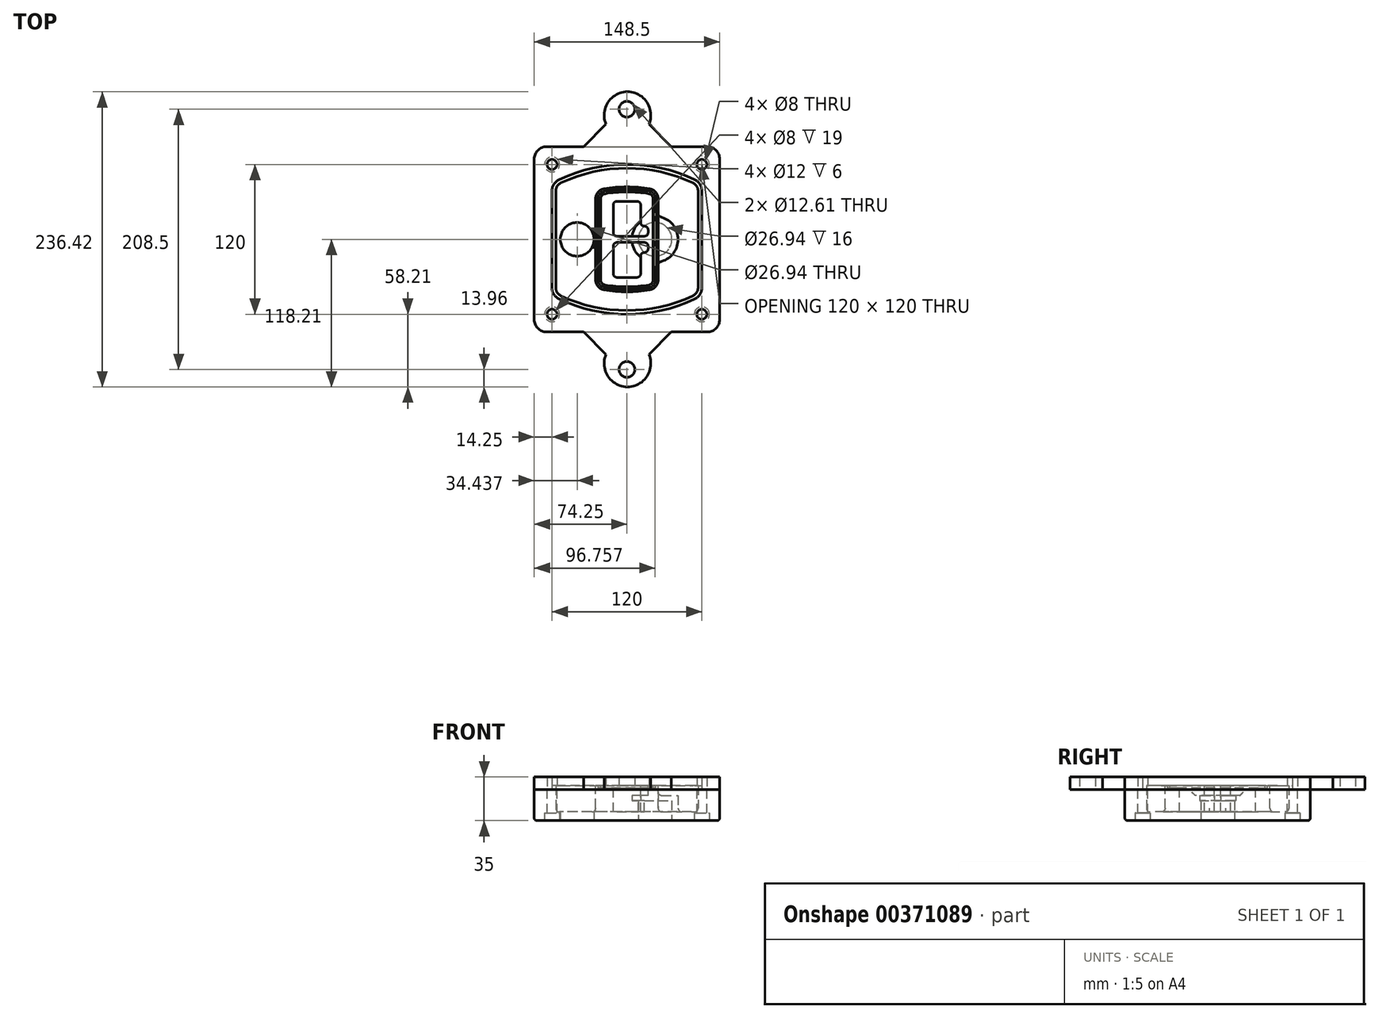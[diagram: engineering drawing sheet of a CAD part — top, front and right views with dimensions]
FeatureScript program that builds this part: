
annotation { "Feature Type Name" : "Feature", "Feature Type Description" : "" }
export const myFeature = defineFeature(function(context is Context, id is Id, definition is map)
    precondition{}
    {
        {
            var Q0;
            Q0=qCreatedBy(makeId("Top.planeOp"),FACE);
            var sketch = newSketch(context, id + "F0", { "sketchPlane" : qUnion([Q0])});
            skPoint(sketch, "E0.rect.middle", {"position": v(0, 0) * mm});
            skLineSegment(sketch, "E1.bottom", {"start": v(-64.25, -74.25) * mm, "end": v(64.25, -74.25) * mm});
            skLineSegment(sketch, "E1.top", {"start": v(-64.25, 74.25) * mm, "end": v(64.25, 74.25) * mm});
            skLineSegment(sketch, "E1.left", {"start": v(-74.25, -64.25) * mm, "end": v(-74.25, 64.25) * mm});
            skLineSegment(sketch, "E1.right", {"start": v(74.25, -64.25) * mm, "end": v(74.25, 64.25) * mm});
            skLineSegment(sketch, "E2", {"start": v(-74.25, 74.25) * mm, "end": v(74.25, -74.25) * mm, "construction": true});
            skLineSegment(sketch, "E3", {"start": v(74.25, 74.25) * mm, "end": v(-74.25, -74.25) * mm, "construction": true});
            skCircle(sketch, "E4", {"center": v(-60, 60) * mm, "radius": 4 * mm});
            skCircle(sketch, "E5", {"center": v(60, 60) * mm, "radius": 4 * mm});
            skCircle(sketch, "E6", {"center": v(60, -60) * mm, "radius": 4 * mm});
            skCircle(sketch, "E7", {"center": v(-60, -60) * mm, "radius": 4 * mm});
            skLineSegment(sketch, "E8", {"start": v(-60, 60) * mm, "end": v(60, 60) * mm, "construction": true});
            skLineSegment(sketch, "E9", {"start": v(60, 60) * mm, "end": v(60, -60) * mm, "construction": true});
            skLineSegment(sketch, "E10", {"start": v(60, -60) * mm, "end": v(-60, -60) * mm, "construction": true});
            skLineSegment(sketch, "E11", {"start": v(-60, -60) * mm, "end": v(-60, 60) * mm, "construction": true});
            skLineSegment(sketch, "E12", {"start": v(-60, 38.83) * mm, "end": v(-60, -38.83) * mm});
            skLineSegment(sketch, "E13", {"start": v(60, 38.83) * mm, "end": v(60, -38.83) * mm});
            skArc(sketch, "E14", {"start": v(54.26, 47.88) * mm, "mid": v(0, 60) * mm, "end": v(-54.26, 47.88) * mm});
            skArc(sketch, "E15", {"start": v(-54.26, -47.88) * mm, "mid": v(0, -60) * mm, "end": v(54.26, -47.88) * mm});
            skLineSegment(sketch, "E16", {"start": v(-60, 0) * mm, "end": v(60, 0) * mm, "construction": true});
            skPoint(sketch, "E17.visualSharp", {"position": v(-60, -45) * mm});
            skArc(sketch, "E17.filletArc", {"start": v(-60, -38.83) * mm, "mid": v(-58.44, -44.2) * mm, "end": v(-54.26, -47.88) * mm});
            skPoint(sketch, "E18.visualSharp", {"position": v(-60, 45) * mm});
            skArc(sketch, "E18.filletArc", {"start": v(-54.26, 47.88) * mm, "mid": v(-58.44, 44.2) * mm, "end": v(-60, 38.83) * mm});
            skPoint(sketch, "E19.visualSharp", {"position": v(60, 45) * mm});
            skArc(sketch, "E19.filletArc", {"start": v(60, 38.83) * mm, "mid": v(58.44, 44.2) * mm, "end": v(54.26, 47.88) * mm});
            skPoint(sketch, "E20.visualSharp", {"position": v(60, -45) * mm});
            skArc(sketch, "E20.filletArc", {"start": v(54.26, -47.88) * mm, "mid": v(58.44, -44.2) * mm, "end": v(60, -38.83) * mm});
            skPoint(sketch, "E21.visualSharp", {"position": v(-74.25, 74.25) * mm});
            skArc(sketch, "E21.filletArc", {"start": v(-64.25, 74.25) * mm, "mid": v(-71.32, 71.32) * mm, "end": v(-74.25, 64.25) * mm});
            skPoint(sketch, "E22.visualSharp", {"position": v(74.25, 74.25) * mm});
            skArc(sketch, "E22.filletArc", {"start": v(74.25, 64.25) * mm, "mid": v(71.32, 71.32) * mm, "end": v(64.25, 74.25) * mm});
            skPoint(sketch, "E23.visualSharp", {"position": v(74.25, -74.25) * mm});
            skArc(sketch, "E23.filletArc", {"start": v(64.25, -74.25) * mm, "mid": v(71.32, -71.32) * mm, "end": v(74.25, -64.25) * mm});
            skPoint(sketch, "E24.visualSharp", {"position": v(-74.25, -74.25) * mm});
            skArc(sketch, "E24.filletArc", {"start": v(-74.25, -64.25) * mm, "mid": v(-71.32, -71.32) * mm, "end": v(-64.25, -74.25) * mm});
            skArc(sketch, "E25.0", {"start": v(57, 38.83) * mm, "mid": v(55.9, 42.58) * mm, "end": v(52.98, 45.17) * mm});
            skLineSegment(sketch, "E25.1", {"start": v(57, 38.83) * mm, "end": v(57, -38.83) * mm});
            skArc(sketch, "E25.2", {"start": v(52.98, -45.17) * mm, "mid": v(55.9, -42.58) * mm, "end": v(57, -38.83) * mm});
            skArc(sketch, "E25.3", {"start": v(-52.98, -45.17) * mm, "mid": v(0, -57) * mm, "end": v(52.98, -45.17) * mm});
            skArc(sketch, "E25.4", {"start": v(-57, -38.83) * mm, "mid": v(-55.9, -42.58) * mm, "end": v(-52.98, -45.17) * mm});
            skArc(sketch, "E25.5", {"start": v(52.98, 45.17) * mm, "mid": v(0, 57) * mm, "end": v(-52.98, 45.17) * mm});
            skLineSegment(sketch, "E25.6", {"start": v(-57, 38.83) * mm, "end": v(-57, -38.83) * mm});
            skArc(sketch, "E25.7", {"start": v(-52.98, 45.17) * mm, "mid": v(-55.9, 42.58) * mm, "end": v(-57, 38.83) * mm});
            skArc(sketch, "E26.0", {"start": v(-55.96, 51.5) * mm, "mid": v(-61.82, 46.33) * mm, "end": v(-64, 38.83) * mm});
            skArc(sketch, "E26.1", {"start": v(55.96, 51.5) * mm, "mid": v(0, 64) * mm, "end": v(-55.96, 51.5) * mm});
            skArc(sketch, "E26.2", {"start": v(64, 38.83) * mm, "mid": v(61.82, 46.33) * mm, "end": v(55.96, 51.5) * mm});
            skLineSegment(sketch, "E26.3", {"start": v(64, 38.83) * mm, "end": v(64, -38.83) * mm});
            skArc(sketch, "E26.4", {"start": v(55.96, -51.5) * mm, "mid": v(61.82, -46.33) * mm, "end": v(64, -38.83) * mm});
            skLineSegment(sketch, "E26.5", {"start": v(-64, 38.83) * mm, "end": v(-64, -38.83) * mm});
            skArc(sketch, "E26.6", {"start": v(-55.96, -51.5) * mm, "mid": v(0, -64) * mm, "end": v(55.96, -51.5) * mm});
            skArc(sketch, "E26.7", {"start": v(-64, -38.83) * mm, "mid": v(-61.82, -46.33) * mm, "end": v(-55.96, -51.5) * mm});
            skSolve(sketch);
        }
        {
            var Q0;
            Q0=makeQuery(id+"F0.imprint","IMPRINT",FACE,{"disambiguationData":[TD([[makeQuery(id+"F0.imprint","IMPRINT",EDGE,{"derivedFrom":sQuery(id+"F0.wireOp",EDGE,"E1.bottom")}),1.0]])]});
            var Q1;
            Q1=makeQuery(id+"F0.imprint","IMPRINT",FACE,{"disambiguationData":[TD([[makeQuery(id+"F0.imprint","IMPRINT",EDGE,{"derivedFrom":sQuery(id+"F0.wireOp",EDGE,"E12")}),1.0]])]});
            var Q2;
            Q2=makeQuery(id+"F0.imprint","IMPRINT",FACE,{"disambiguationData":[TD([[makeQuery(id+"F0.imprint","IMPRINT",EDGE,{"derivedFrom":sQuery(id+"F0.wireOp",EDGE,"E25.0")}),1.0]])]});
            var Q3;
            Q3=makeQuery(id+"F0.imprint","IMPRINT",FACE,{"disambiguationData":[TD([[makeQuery(id+"F0.imprint","IMPRINT",EDGE,{"derivedFrom":sQuery(id+"F0.wireOp",EDGE,"E12")}),-1.0]])]});
            extrude(context, id + "F1", {"entities" : qUnion([Q0, Q1, Q2, Q3]), "oppositeDirection" : true, "depth" : 25 * mm});
        }
        {
            var Q0;
            Q0=makeQuery(id+"F0.imprint","IMPRINT",FACE,{"disambiguationData":[TD([[makeQuery(id+"F0.imprint","IMPRINT",EDGE,{"derivedFrom":sQuery(id+"F0.wireOp",EDGE,"E12")}),1.0]])]});
            extrude(context, id + "F2", {"entities" : qUnion([Q0]), "operationType" : NewBodyOperationType.ADD, "depth" : 3 * mm});
        }
        {
            var Q0;
            Q0=makeQuery(id+"F0.imprint","IMPRINT",FACE,{"disambiguationData":[TD([[makeQuery(id+"F0.imprint","IMPRINT",EDGE,{"derivedFrom":sQuery(id+"F0.wireOp",EDGE,"E25.0")}),1.0]])]});
            extrude(context, id + "F3", {"entities" : qUnion([Q0]), "operationType" : NewBodyOperationType.REMOVE, "oppositeDirection" : true, "depth" : 18 * mm});
        }
        {
            var Q0;
            Q0=makeQuery(id+"F2.opExtrude","CAP_FACE",FACE,{"disambiguationData":[OSD([sQuery(id+"F0.wireOp",EDGE,"E12"),sQuery(id+"F0.wireOp",EDGE,"E13"),sQuery(id+"F0.wireOp",EDGE,"E14"),sQuery(id+"F0.wireOp",EDGE,"E15"),sQuery(id+"F0.wireOp",EDGE,"E17.filletArc"),sQuery(id+"F0.wireOp",EDGE,"E18.filletArc"),sQuery(id+"F0.wireOp",EDGE,"E19.filletArc"),sQuery(id+"F0.wireOp",EDGE,"E20.filletArc"),sQuery(id+"F0.wireOp",EDGE,"E25.0"),sQuery(id+"F0.wireOp",EDGE,"E25.1"),sQuery(id+"F0.wireOp",EDGE,"E25.2"),sQuery(id+"F0.wireOp",EDGE,"E25.3"),sQuery(id+"F0.wireOp",EDGE,"E25.4"),sQuery(id+"F0.wireOp",EDGE,"E25.5"),sQuery(id+"F0.wireOp",EDGE,"E25.6"),sQuery(id+"F0.wireOp",EDGE,"E25.7")])],"isStart":false});
            var sketch = newSketch(context, id + "F4", { "sketchPlane" : qUnion([Q0])});
            skArc(sketch, "E27.0", {"start": v(-18.34, -40.45) * mm, "mid": v(0, -42) * mm, "end": v(18.34, -40.45) * mm});
            skArc(sketch, "E28.0", {"start": v(18.34, 40.45) * mm, "mid": v(0, 42) * mm, "end": v(-18.34, 40.45) * mm});
            skLineSegment(sketch, "E29", {"start": v(-25, 32.57) * mm, "end": v(-25, -32.57) * mm});
            skLineSegment(sketch, "E30", {"start": v(25, 32.57) * mm, "end": v(25, -32.57) * mm});
            skLineSegment(sketch, "E31", {"start": v(-25, 39.1) * mm, "end": v(25, 39.1) * mm, "construction": true});
            skLineSegment(sketch, "E32", {"start": v(-25, -39.1) * mm, "end": v(25, -39.1) * mm, "construction": true});
            skPoint(sketch, "E33.visualSharp", {"position": v(-25, 39.1) * mm});
            skArc(sketch, "E33.filletArc", {"start": v(-18.34, 40.45) * mm, "mid": v(-23.11, 37.73) * mm, "end": v(-25, 32.57) * mm});
            skPoint(sketch, "E34.visualSharp", {"position": v(25, 39.1) * mm});
            skArc(sketch, "E34.filletArc", {"start": v(25, 32.57) * mm, "mid": v(23.11, 37.73) * mm, "end": v(18.34, 40.45) * mm});
            skPoint(sketch, "E35.visualSharp", {"position": v(25, -39.1) * mm});
            skArc(sketch, "E35.filletArc", {"start": v(18.34, -40.45) * mm, "mid": v(23.11, -37.73) * mm, "end": v(25, -32.57) * mm});
            skPoint(sketch, "E36.visualSharp", {"position": v(-25, -39.1) * mm});
            skArc(sketch, "E36.filletArc", {"start": v(-25, -32.57) * mm, "mid": v(-23.11, -37.73) * mm, "end": v(-18.34, -40.45) * mm});
            skArc(sketch, "E37.0", {"start": v(52.98, 45.17) * mm, "mid": v(0, 57) * mm, "end": v(-52.98, 45.17) * mm});
            skArc(sketch, "E37.1", {"start": v(-52.98, 45.17) * mm, "mid": v(-55.9, 42.58) * mm, "end": v(-57, 38.83) * mm});
            skLineSegment(sketch, "E37.2", {"start": v(-57, 38.83) * mm, "end": v(-57, -38.83) * mm});
            skArc(sketch, "E37.3", {"start": v(-57, -38.83) * mm, "mid": v(-55.9, -42.58) * mm, "end": v(-52.98, -45.17) * mm});
            skArc(sketch, "E37.4", {"start": v(-52.98, -45.17) * mm, "mid": v(0, -57) * mm, "end": v(52.98, -45.17) * mm});
            skArc(sketch, "E37.5", {"start": v(52.98, -45.17) * mm, "mid": v(55.9, -42.58) * mm, "end": v(57, -38.83) * mm});
            skLineSegment(sketch, "E37.6", {"start": v(57, 38.83) * mm, "end": v(57, -38.83) * mm});
            skArc(sketch, "E37.7", {"start": v(57, 38.83) * mm, "mid": v(55.9, 42.58) * mm, "end": v(52.98, 45.17) * mm});
            skLineSegment(sketch, "E38.0", {"start": v(23, 32.57) * mm, "end": v(23, -32.57) * mm});
            skArc(sketch, "E38.1", {"start": v(18, -38.48) * mm, "mid": v(21.58, -36.44) * mm, "end": v(23, -32.57) * mm});
            skArc(sketch, "E38.2", {"start": v(-18, -38.48) * mm, "mid": v(0, -40) * mm, "end": v(18, -38.48) * mm});
            skArc(sketch, "E38.3", {"start": v(-23, -32.57) * mm, "mid": v(-21.58, -36.44) * mm, "end": v(-18, -38.48) * mm});
            skLineSegment(sketch, "E38.4", {"start": v(-23, 32.57) * mm, "end": v(-23, -32.57) * mm});
            skArc(sketch, "E38.5", {"start": v(23, 32.57) * mm, "mid": v(21.58, 36.44) * mm, "end": v(18, 38.48) * mm});
            skArc(sketch, "E38.6", {"start": v(-18, 38.48) * mm, "mid": v(-21.58, 36.44) * mm, "end": v(-23, 32.57) * mm});
            skArc(sketch, "E38.7", {"start": v(18, 38.48) * mm, "mid": v(0, 40) * mm, "end": v(-18, 38.48) * mm});
            skArc(sketch, "E39.0", {"start": v(21, 32.57) * mm, "mid": v(20.06, 35.15) * mm, "end": v(17.67, 36.5) * mm});
            skLineSegment(sketch, "E39.1", {"start": v(21, 32.57) * mm, "end": v(21, -32.57) * mm});
            skArc(sketch, "E39.2", {"start": v(17.67, -36.5) * mm, "mid": v(20.06, -35.15) * mm, "end": v(21, -32.57) * mm});
            skArc(sketch, "E39.3", {"start": v(-17.67, -36.5) * mm, "mid": v(0, -38) * mm, "end": v(17.67, -36.5) * mm});
            skArc(sketch, "E39.4", {"start": v(-21, -32.57) * mm, "mid": v(-20.06, -35.15) * mm, "end": v(-17.67, -36.5) * mm});
            skArc(sketch, "E39.5", {"start": v(17.67, 36.5) * mm, "mid": v(0, 38) * mm, "end": v(-17.67, 36.5) * mm});
            skLineSegment(sketch, "E39.6", {"start": v(-21, 32.57) * mm, "end": v(-21, -32.57) * mm});
            skArc(sketch, "E39.7", {"start": v(-17.67, 36.5) * mm, "mid": v(-20.06, 35.15) * mm, "end": v(-21, 32.57) * mm});
            skLineSegment(sketch, "E40", {"start": v(-25, 0) * mm, "end": v(25, 0) * mm, "construction": true});
            skLineSegment(sketch, "E41", {"start": v(-11, 5.5) * mm, "end": v(-11, 27.5) * mm});
            skLineSegment(sketch, "E42", {"start": v(-8, 30.5) * mm, "end": v(8, 30.5) * mm});
            skLineSegment(sketch, "E43", {"start": v(11, 27.5) * mm, "end": v(11, 13.5) * mm});
            skLineSegment(sketch, "E44", {"start": v(14, 10.5) * mm, "end": v(14, 10.5) * mm});
            skLineSegment(sketch, "E45", {"start": v(17, 7.5) * mm, "end": v(17, 5.5) * mm});
            skLineSegment(sketch, "E46", {"start": v(14, 2.5) * mm, "end": v(-8, 2.5) * mm});
            skPoint(sketch, "E47.visualSharp", {"position": v(-11, 30.5) * mm});
            skArc(sketch, "E47.filletArc", {"start": v(-8, 30.5) * mm, "mid": v(-10.12, 29.62) * mm, "end": v(-11, 27.5) * mm});
            skPoint(sketch, "E48.visualSharp", {"position": v(11, 30.5) * mm});
            skArc(sketch, "E48.filletArc", {"start": v(11, 27.5) * mm, "mid": v(10.12, 29.62) * mm, "end": v(8, 30.5) * mm});
            skPoint(sketch, "E49.visualSharp", {"position": v(11, 10.5) * mm});
            skArc(sketch, "E49.filletArc", {"start": v(11, 13.5) * mm, "mid": v(11.88, 11.38) * mm, "end": v(14, 10.5) * mm});
            skPoint(sketch, "E50.visualSharp", {"position": v(17, 10.5) * mm});
            skArc(sketch, "E50.filletArc", {"start": v(17, 7.5) * mm, "mid": v(16.12, 9.62) * mm, "end": v(14, 10.5) * mm});
            skPoint(sketch, "E51.visualSharp", {"position": v(17, 2.5) * mm});
            skArc(sketch, "E51.filletArc", {"start": v(14, 2.5) * mm, "mid": v(16.12, 3.38) * mm, "end": v(17, 5.5) * mm});
            skPoint(sketch, "E52.visualSharp", {"position": v(-11, 2.5) * mm});
            skArc(sketch, "E52.filletArc", {"start": v(-11, 5.5) * mm, "mid": v(-10.12, 3.38) * mm, "end": v(-8, 2.5) * mm});
            skLineSegment(sketch, "E53.0.MirrorCS", {"start": v(14, -2.5) * mm, "end": v(-8, -2.5) * mm});
            skArc(sketch, "E54.0.MirrorCS", {"start": v(-11, -5.5) * mm, "mid": v(-10.12, -3.38) * mm, "end": v(-8, -2.5) * mm});
            skLineSegment(sketch, "E55.0.MirrorCS", {"start": v(-11, -5.5) * mm, "end": v(-11, -27.5) * mm});
            skArc(sketch, "E56.0.MirrorCS", {"start": v(-8, -30.5) * mm, "mid": v(-10.12, -29.62) * mm, "end": v(-11, -27.5) * mm});
            skLineSegment(sketch, "E57.0.MirrorCS", {"start": v(-8, -30.5) * mm, "end": v(8, -30.5) * mm});
            skArc(sketch, "E58.0.MirrorCS", {"start": v(11, -27.5) * mm, "mid": v(10.12, -29.62) * mm, "end": v(8, -30.5) * mm});
            skLineSegment(sketch, "E59.0.MirrorCS", {"start": v(11, -27.5) * mm, "end": v(11, -13.5) * mm});
            skArc(sketch, "E60.0.MirrorCS", {"start": v(11, -13.5) * mm, "mid": v(11.88, -11.38) * mm, "end": v(14, -10.5) * mm});
            skArc(sketch, "E61.0.MirrorCS", {"start": v(17, -7.5) * mm, "mid": v(16.12, -9.62) * mm, "end": v(14, -10.5) * mm});
            skLineSegment(sketch, "E62.0.MirrorCS", {"start": v(17, -7.5) * mm, "end": v(17, -5.5) * mm});
            skArc(sketch, "E63.0.MirrorCS", {"start": v(14, -2.5) * mm, "mid": v(16.12, -3.38) * mm, "end": v(17, -5.5) * mm});
            skSolve(sketch);
        }
        {
            var Q0;
            Q0=makeQuery(id+"F4.imprint","IMPRINT",FACE,{"disambiguationData":[TD([[makeQuery(id+"F4.imprint","IMPRINT",EDGE,{"derivedFrom":sQuery(id+"F4.wireOp",EDGE,"E27.0")}),1.0]])]});
            var Q1;
            Q1=makeQuery(id+"F4.imprint","IMPRINT",FACE,{"disambiguationData":[TD([[makeQuery(id+"F4.imprint","IMPRINT",EDGE,{"derivedFrom":sQuery(id+"F4.wireOp",EDGE,"E38.0")}),-1.0]])]});
            var Q2;
            Q2=makeQuery(id+"F4.imprint","IMPRINT",FACE,{"disambiguationData":[TD([[makeQuery(id+"F4.imprint","IMPRINT",EDGE,{"derivedFrom":sQuery(id+"F4.wireOp",EDGE,"E39.0")}),1.0]])]});
            extrude(context, id + "F5", {"entities" : qUnion([Q0, Q1, Q2]), "operationType" : NewBodyOperationType.ADD, "endBound" : BoundingType.UP_TO_NEXT, "oppositeDirection" : true, "depth" : 25 * mm});
        }
        {
            var Q0;
            Q0=makeQuery(id+"F4.imprint","IMPRINT",FACE,{"disambiguationData":[TD([[makeQuery(id+"F4.imprint","IMPRINT",EDGE,{"derivedFrom":sQuery(id+"F4.wireOp",EDGE,"E38.0")}),-1.0]])]});
            extrude(context, id + "F6", {"entities" : qUnion([Q0]), "operationType" : NewBodyOperationType.REMOVE, "oppositeDirection" : true, "depth" : 2 * mm});
        }
        {
            var Q0;
            Q0=makeQuery(id+"F1.opExtrude","CAP_FACE",FACE,{"disambiguationData":[OSD([sQuery(id+"F0.wireOp",EDGE,"E1.bottom"),sQuery(id+"F0.wireOp",EDGE,"E1.top"),sQuery(id+"F0.wireOp",EDGE,"E1.left"),sQuery(id+"F0.wireOp",EDGE,"E1.right"),sQuery(id+"F0.wireOp",EDGE,"E4"),sQuery(id+"F0.wireOp",EDGE,"E5"),sQuery(id+"F0.wireOp",EDGE,"E6"),sQuery(id+"F0.wireOp",EDGE,"E7"),sQuery(id+"F0.wireOp",EDGE,"E21.filletArc"),sQuery(id+"F0.wireOp",EDGE,"E22.filletArc"),sQuery(id+"F0.wireOp",EDGE,"E23.filletArc"),sQuery(id+"F0.wireOp",EDGE,"E24.filletArc")])],"isStart":false});
            var sketch = newSketch(context, id + "F7", { "sketchPlane" : qUnion([Q0])});
            skCircle(sketch, "E64", {"center": v(22.5, 0) * mm, "radius": 13.47 * mm});
            skCircle(sketch, "E65", {"center": v(-39.81, 0) * mm, "radius": 13.47 * mm});
            skLineSegment(sketch, "E66", {"start": v(74.25, 0) * mm, "end": v(-74.25, 0) * mm});
            skCircle(sketch, "E67", {"center": v(22.5, 0) * mm, "radius": 18.47 * mm});
            skCircle(sketch, "E68", {"center": v(60, -60) * mm, "radius": 6 * mm});
            skCircle(sketch, "E69", {"center": v(-60, -60) * mm, "radius": 6 * mm});
            skCircle(sketch, "E70", {"center": v(-60, 60) * mm, "radius": 6 * mm});
            skCircle(sketch, "E71", {"center": v(60, 60) * mm, "radius": 6 * mm});
            skSolve(sketch);
        }
        {
            var Q0;
            {var subQ1=sQuery(id+"F7.wireOp",EDGE,"E66");var subQ4=sQuery(id+"F7.wireOp",EDGE,"E64");var subQ6=makeQuery(id+"F7.imprint","INTERSECT",VERTEX,{"disambiguationData":[OD(0.0)],"derivedFrom":[subQ4,subQ1]});Q0=makeQuery(id+"F7.imprint","IMPRINT",FACE,{"disambiguationData":[TD([[makeQuery(id+"F7.imprint","IMPRINT",EDGE,{"disambiguationData":[TD([[subQ6,-1.0]])],"derivedFrom":subQ4}),-1.0]])]});}
            var Q1;
            {var subQ0=sQuery(id+"F7.wireOp",EDGE,"E66");var subQ1=sQuery(id+"F7.wireOp",EDGE,"E64");var subQ3=makeQuery(id+"F7.imprint","INTERSECT",VERTEX,{"disambiguationData":[OD(0.0)],"derivedFrom":[subQ1,subQ0]});Q1=makeQuery(id+"F7.imprint","IMPRINT",FACE,{"disambiguationData":[TD([[makeQuery(id+"F7.imprint","IMPRINT",EDGE,{"disambiguationData":[TD([[subQ3,-1.0]])],"derivedFrom":subQ1}),1.0]])]});}
            var Q2;
            {var subQ0=sQuery(id+"F7.wireOp",EDGE,"E66");var subQ1=sQuery(id+"F7.wireOp",EDGE,"E64");var subQ3=makeQuery(id+"F7.imprint","INTERSECT",VERTEX,{"disambiguationData":[OD(0.0)],"derivedFrom":[subQ1,subQ0]});Q2=makeQuery(id+"F7.imprint","IMPRINT",FACE,{"disambiguationData":[TD([[makeQuery(id+"F7.imprint","IMPRINT",EDGE,{"disambiguationData":[TD([[subQ3,1.0]])],"derivedFrom":subQ1}),1.0]])]});}
            var Q3;
            {var subQ1=sQuery(id+"F7.wireOp",EDGE,"E66");var subQ4=sQuery(id+"F7.wireOp",EDGE,"E64");var subQ6=makeQuery(id+"F7.imprint","INTERSECT",VERTEX,{"disambiguationData":[OD(0.0)],"derivedFrom":[subQ4,subQ1]});Q3=makeQuery(id+"F7.imprint","IMPRINT",FACE,{"disambiguationData":[TD([[makeQuery(id+"F7.imprint","IMPRINT",EDGE,{"disambiguationData":[TD([[subQ6,1.0]])],"derivedFrom":subQ4}),-1.0]])]});}
            extrude(context, id + "F8", {"entities" : qUnion([Q0, Q1, Q2, Q3]), "operationType" : NewBodyOperationType.ADD, "oppositeDirection" : true, "depth" : 20 * mm});
        }
        {
            var Q0;
            {var subQ0=sQuery(id+"F7.wireOp",EDGE,"E66");var subQ1=sQuery(id+"F7.wireOp",EDGE,"E64");var subQ3=makeQuery(id+"F7.imprint","INTERSECT",VERTEX,{"disambiguationData":[OD(0.0)],"derivedFrom":[subQ1,subQ0]});Q0=makeQuery(id+"F7.imprint","IMPRINT",FACE,{"disambiguationData":[TD([[makeQuery(id+"F7.imprint","IMPRINT",EDGE,{"disambiguationData":[TD([[subQ3,-1.0]])],"derivedFrom":subQ1}),1.0]])]});}
            var Q1;
            {var subQ0=sQuery(id+"F7.wireOp",EDGE,"E66");var subQ1=sQuery(id+"F7.wireOp",EDGE,"E64");var subQ3=makeQuery(id+"F7.imprint","INTERSECT",VERTEX,{"disambiguationData":[OD(0.0)],"derivedFrom":[subQ1,subQ0]});Q1=makeQuery(id+"F7.imprint","IMPRINT",FACE,{"disambiguationData":[TD([[makeQuery(id+"F7.imprint","IMPRINT",EDGE,{"disambiguationData":[TD([[subQ3,1.0]])],"derivedFrom":subQ1}),1.0]])]});}
            extrude(context, id + "F9", {"entities" : qUnion([Q0, Q1]), "operationType" : NewBodyOperationType.REMOVE, "oppositeDirection" : true, "depth" : 16 * mm});
        }
        {
            var Q0;
            {var subQ0=sQuery(id+"F7.wireOp",EDGE,"E66");var subQ1=sQuery(id+"F7.wireOp",EDGE,"E65");var subQ3=makeQuery(id+"F7.imprint","INTERSECT",VERTEX,{"disambiguationData":[OD(0.0)],"derivedFrom":[subQ1,subQ0]});Q0=makeQuery(id+"F7.imprint","IMPRINT",FACE,{"disambiguationData":[TD([[makeQuery(id+"F7.imprint","IMPRINT",EDGE,{"disambiguationData":[TD([[subQ3,-1.0]])],"derivedFrom":subQ1}),1.0]])]});}
            var Q1;
            {var subQ0=sQuery(id+"F7.wireOp",EDGE,"E66");var subQ1=sQuery(id+"F7.wireOp",EDGE,"E65");var subQ3=makeQuery(id+"F7.imprint","INTERSECT",VERTEX,{"disambiguationData":[OD(0.0)],"derivedFrom":[subQ1,subQ0]});Q1=makeQuery(id+"F7.imprint","IMPRINT",FACE,{"disambiguationData":[TD([[makeQuery(id+"F7.imprint","IMPRINT",EDGE,{"disambiguationData":[TD([[subQ3,1.0]])],"derivedFrom":subQ1}),1.0]])]});}
            extrude(context, id + "F10", {"entities" : qUnion([Q0, Q1]), "operationType" : NewBodyOperationType.REMOVE, "oppositeDirection" : true, "depth" : 25 * mm});
        }
        {
            var Q0;
            Q0=makeQuery(id+"F7.imprint","IMPRINT",FACE,{"disambiguationData":[TD([[makeQuery(id+"F7.imprint","IMPRINT",EDGE,{"derivedFrom":sQuery(id+"F7.wireOp",EDGE,"E68")}),1.0]])]});
            var Q1;
            Q1=makeQuery(id+"F7.imprint","IMPRINT",FACE,{"disambiguationData":[TD([[makeQuery(id+"F7.imprint","IMPRINT",EDGE,{"derivedFrom":makeQuery(id+"F1.opExtrude","CAP_EDGE",EDGE,{"disambiguationData":[OSD([sQuery(id+"F0.wireOp",EDGE,"E5")])],"isStart":false})}),-1.0]])]});
            var Q2;
            Q2=makeQuery(id+"F7.imprint","IMPRINT",FACE,{"disambiguationData":[TD([[makeQuery(id+"F7.imprint","IMPRINT",EDGE,{"derivedFrom":sQuery(id+"F7.wireOp",EDGE,"E69")}),1.0]])]});
            var Q3;
            Q3=makeQuery(id+"F7.imprint","IMPRINT",FACE,{"disambiguationData":[TD([[makeQuery(id+"F7.imprint","IMPRINT",EDGE,{"derivedFrom":makeQuery(id+"F1.opExtrude","CAP_EDGE",EDGE,{"disambiguationData":[OSD([sQuery(id+"F0.wireOp",EDGE,"E4")])],"isStart":false})}),-1.0]])]});
            var Q4;
            Q4=makeQuery(id+"F7.imprint","IMPRINT",FACE,{"disambiguationData":[TD([[makeQuery(id+"F7.imprint","IMPRINT",EDGE,{"derivedFrom":sQuery(id+"F7.wireOp",EDGE,"E70")}),1.0]])]});
            var Q5;
            Q5=makeQuery(id+"F7.imprint","IMPRINT",FACE,{"disambiguationData":[TD([[makeQuery(id+"F7.imprint","IMPRINT",EDGE,{"derivedFrom":makeQuery(id+"F1.opExtrude","CAP_EDGE",EDGE,{"disambiguationData":[OSD([sQuery(id+"F0.wireOp",EDGE,"E7")])],"isStart":false})}),-1.0]])]});
            var Q6;
            Q6=makeQuery(id+"F7.imprint","IMPRINT",FACE,{"disambiguationData":[TD([[makeQuery(id+"F7.imprint","IMPRINT",EDGE,{"derivedFrom":sQuery(id+"F7.wireOp",EDGE,"E71")}),1.0]])]});
            var Q7;
            Q7=makeQuery(id+"F7.imprint","IMPRINT",FACE,{"disambiguationData":[TD([[makeQuery(id+"F7.imprint","IMPRINT",EDGE,{"derivedFrom":makeQuery(id+"F1.opExtrude","CAP_EDGE",EDGE,{"disambiguationData":[OSD([sQuery(id+"F0.wireOp",EDGE,"E6")])],"isStart":false})}),-1.0]])]});
            extrude(context, id + "F11", {"entities" : qUnion([Q0, Q1, Q2, Q3, Q4, Q5, Q6, Q7]), "operationType" : NewBodyOperationType.REMOVE, "oppositeDirection" : true, "depth" : 6 * mm});
        }
        {
            var Q0;
            Q0=makeQuery(id+"F9.boolean.opBoolean","COPY",FACE,{"derivedFrom":makeQuery(id+"F9.opExtrude","CAP_FACE",FACE,{"disambiguationData":[OSD([sQuery(id+"F7.wireOp",EDGE,"E64")])],"isStart":false})});
            var sketch = newSketch(context, id + "F12", { "sketchPlane" : qUnion([Q0])});
            skArc(sketch, "E72.0", {"start": v(11, 14.45) * mm, "mid": v(6.45, 9.13) * mm, "end": v(4.2, 2.5) * mm});
            skArc(sketch, "E72.1", {"start": v(4.2, -2.5) * mm, "mid": v(6.45, -9.13) * mm, "end": v(11, -14.45) * mm});
            skLineSegment(sketch, "E73", {"start": v(4.2, -2.5) * mm, "end": v(14, -2.5) * mm});
            skLineSegment(sketch, "E74.0", {"start": v(14, 2.5) * mm, "end": v(4.2, 2.5) * mm});
            skArc(sketch, "E74.1", {"start": v(14, 2.5) * mm, "mid": v(16.12, 3.38) * mm, "end": v(17, 5.5) * mm});
            skLineSegment(sketch, "E74.2", {"start": v(17, 7.5) * mm, "end": v(17, 5.5) * mm});
            skArc(sketch, "E74.3", {"start": v(17, 7.5) * mm, "mid": v(16.12, 9.62) * mm, "end": v(14, 10.5) * mm});
            skArc(sketch, "E74.4", {"start": v(11, 13.5) * mm, "mid": v(11.88, 11.38) * mm, "end": v(14, 10.5) * mm});
            skLineSegment(sketch, "E74.5", {"start": v(11, 14.45) * mm, "end": v(11, 13.5) * mm});
            skLineSegment(sketch, "E74.7", {"start": v(14, -2.5) * mm, "end": v(4.2, -2.5) * mm});
            skArc(sketch, "E74.8", {"start": v(14, -2.5) * mm, "mid": v(16.12, -3.38) * mm, "end": v(17, -5.5) * mm});
            skLineSegment(sketch, "E74.9", {"start": v(17, -7.5) * mm, "end": v(17, -5.5) * mm});
            skArc(sketch, "E74.10", {"start": v(17, -7.5) * mm, "mid": v(16.12, -9.62) * mm, "end": v(14, -10.5) * mm});
            skArc(sketch, "E74.11", {"start": v(11, -13.5) * mm, "mid": v(11.88, -11.38) * mm, "end": v(14, -10.5) * mm});
            skLineSegment(sketch, "E74.12", {"start": v(11, -14.45) * mm, "end": v(11, -13.5) * mm});
            skPoint(sketch, "E75.orphan", {"position": v(11, -27.5) * mm});
            skPoint(sketch, "E76.orphan", {"position": v(-8, -2.5) * mm});
            skPoint(sketch, "E77.orphan", {"position": v(-8, 2.5) * mm});
            skPoint(sketch, "E78.orphan", {"position": v(11, 27.5) * mm});
            skSolve(sketch);
        }
        {
            var Q0;
            {var subQ7=sQuery(id+"F12.wireOp",EDGE,"E72.0");var subQ14=sQuery(id+"F12.wireOp",EDGE,"E72.1");var subQ16=sQuery(id+"F12.wireOp",EDGE,"E74.1");var subQ18=sQuery(id+"F12.wireOp",EDGE,"E74.8");Q0=qUnion([makeQuery(id+"F12.imprint","IMPRINT",FACE,{"disambiguationData":[TD([[makeQuery(id+"F12.imprint","IMPRINT",EDGE,{"derivedFrom":subQ7}),1.0]])]}),makeQuery(id+"F12.imprint","IMPRINT",FACE,{"disambiguationData":[TD([[makeQuery(id+"F12.imprint","IMPRINT",EDGE,{"derivedFrom":subQ14}),1.0]])]}),makeQuery(id+"F12.imprint","IMPRINT",FACE,{"disambiguationData":[TD([[makeQuery(id+"F12.imprint","IMPRINT",EDGE,{"derivedFrom":subQ16}),1.0]])]}),makeQuery(id+"F12.imprint","IMPRINT",FACE,{"disambiguationData":[TD([[makeQuery(id+"F12.imprint","IMPRINT",EDGE,{"derivedFrom":subQ18}),-1.0]])]})]);}
            var Q1;
            Q1=makeQuery(id+"F5.boolean.opBoolean","SPLIT",FACE,{"disambiguationData":[TD([makeQuery(id+"F5.opExtrude","SWEPT_FACE",FACE,{"disambiguationData":[OSD([sQuery(id+"F4.wireOp",EDGE,"E41")])]})])],"derivedFrom":makeQuery(id+"F3.boolean.opBoolean","COPY",FACE,{"derivedFrom":makeQuery(id+"F3.opExtrude","CAP_FACE",FACE,{"disambiguationData":[OSD([sQuery(id+"F0.wireOp",EDGE,"E25.0"),sQuery(id+"F0.wireOp",EDGE,"E25.1"),sQuery(id+"F0.wireOp",EDGE,"E25.2"),sQuery(id+"F0.wireOp",EDGE,"E25.3"),sQuery(id+"F0.wireOp",EDGE,"E25.4"),sQuery(id+"F0.wireOp",EDGE,"E25.5"),sQuery(id+"F0.wireOp",EDGE,"E25.6"),sQuery(id+"F0.wireOp",EDGE,"E25.7")])],"isStart":false})})});
            extrude(context, id + "F13", {"entities" : qUnion([Q0]), "operationType" : NewBodyOperationType.REMOVE, "endBound" : BoundingType.UP_TO_SURFACE, "endBoundEntityFace" : qUnion([Q1]), "depth" : 25 * mm});
        }
        {
            var Q0;
            Q0=makeQuery(id+"F3.boolean.opBoolean","COPY",EDGE,{"derivedFrom":makeQuery(id+"F3.opExtrude","CAP_EDGE",EDGE,{"disambiguationData":[OSD([sQuery(id+"F0.wireOp",EDGE,"E25.6")])],"isStart":false})});
            var Q1;
            Q1=makeQuery(id+"F8.boolean.opBoolean","INTERSECT",EDGE,{"derivedFrom":[makeQuery(id+"F5.opExtrude","SWEPT_FACE",FACE,{"disambiguationData":[OSD([sQuery(id+"F4.wireOp",EDGE,"E30")])]}),makeQuery(id+"F8.opExtrude","CAP_FACE",FACE,{"disambiguationData":[OSD([sQuery(id+"F7.wireOp",EDGE,"E67")])],"isStart":false})]});
            var Q2;
            Q2=makeQuery(id+"F8.boolean.opBoolean","INTERSECT",EDGE,{"disambiguationData":[OD(1.0)],"derivedFrom":[makeQuery(id+"F5.opExtrude","SWEPT_FACE",FACE,{"disambiguationData":[OSD([sQuery(id+"F4.wireOp",EDGE,"E30")])]}),makeQuery(id+"F8.opExtrude","SWEPT_FACE",FACE,{"disambiguationData":[OSD([sQuery(id+"F7.wireOp",EDGE,"E67")])]})]});
            var Q3;
            {var subQ0=sQuery(id+"F4.wireOp",EDGE,"E30");Q3=makeQuery(id+"F8.boolean.opBoolean","SPLIT",EDGE,{"disambiguationData":[TD([makeQuery(id+"F5.opExtrude","SWEPT_FACE",FACE,{"disambiguationData":[OSD([sQuery(id+"F4.wireOp",EDGE,"E35.filletArc")])]})])],"derivedFrom":makeQuery(id+"F5.opExtrude","CAP_EDGE",EDGE,{"disambiguationData":[OSD([subQ0])],"isStart":false})});}
            var Q4;
            {var subQ0=sQuery(id+"F0.wireOp",EDGE,"E25.7");var subQ1=sQuery(id+"F0.wireOp",EDGE,"E25.1");var subQ2=sQuery(id+"F0.wireOp",EDGE,"E25.6");var subQ3=sQuery(id+"F0.wireOp",EDGE,"E25.5");var subQ4=sQuery(id+"F0.wireOp",EDGE,"E25.4");var subQ5=sQuery(id+"F0.wireOp",EDGE,"E25.0");var subQ6=sQuery(id+"F0.wireOp",EDGE,"E25.2");var subQ7=sQuery(id+"F0.wireOp",EDGE,"E25.3");Q4=makeQuery(id+"F8.boolean.opBoolean","INTERSECT",EDGE,{"derivedFrom":[makeQuery(id+"F5.boolean.opBoolean","SPLIT",FACE,{"disambiguationData":[TD([makeQuery(id+"F2.opExtrude","SWEPT_FACE",FACE,{"disambiguationData":[OSD([subQ5])]})])],"derivedFrom":makeQuery(id+"F3.boolean.opBoolean","COPY",FACE,{"derivedFrom":makeQuery(id+"F3.opExtrude","CAP_FACE",FACE,{"disambiguationData":[OSD([subQ5,subQ1,subQ6,subQ7,subQ4,subQ3,subQ2,subQ0])],"isStart":false})})}),makeQuery(id+"F8.opExtrude","SWEPT_FACE",FACE,{"disambiguationData":[OSD([sQuery(id+"F7.wireOp",EDGE,"E67")])]})]});}
            var Q5;
            Q5=makeQuery(id+"F8.boolean.opBoolean","INTERSECT",EDGE,{"disambiguationData":[OD(0.0)],"derivedFrom":[makeQuery(id+"F5.opExtrude","SWEPT_FACE",FACE,{"disambiguationData":[OSD([sQuery(id+"F4.wireOp",EDGE,"E30")])]}),makeQuery(id+"F8.opExtrude","SWEPT_FACE",FACE,{"disambiguationData":[OSD([sQuery(id+"F7.wireOp",EDGE,"E67")])]})]});
            fillet(context, id + "F14", {"entities" : qUnion([Q0, Q1, Q2, Q3, Q4, Q5]), "radius" : 3 * mm, "tangentPropagation" : true, "allowEdgeOverflow" : false});
        }
        {
            var Q0;
            Q0=makeQuery(id+"F1.opExtrude","CAP_EDGE",EDGE,{"disambiguationData":[OSD([sQuery(id+"F0.wireOp",EDGE,"E1.bottom")])],"isStart":false});
            fillet(context, id + "F15", {"entities" : qUnion([Q0]), "radius" : 2 * mm, "tangentPropagation" : true, "allowEdgeOverflow" : false});
        }
        {
            var Q0;
            {var subQ0=sQuery(id+"F0.wireOp",EDGE,"E21.filletArc");var subQ1=sQuery(id+"F0.wireOp",EDGE,"E7");var subQ2=sQuery(id+"F0.wireOp",EDGE,"E6");var subQ3=sQuery(id+"F0.wireOp",EDGE,"E5");var subQ4=sQuery(id+"F0.wireOp",EDGE,"E4");var subQ5=sQuery(id+"F0.wireOp",EDGE,"E22.filletArc");var subQ6=sQuery(id+"F0.wireOp",EDGE,"E1.bottom");var subQ7=sQuery(id+"F0.wireOp",EDGE,"E1.right");var subQ8=sQuery(id+"F0.wireOp",EDGE,"E1.top");var subQ9=sQuery(id+"F0.wireOp",EDGE,"E1.left");var subQ10=sQuery(id+"F0.wireOp",EDGE,"E23.filletArc");var subQ11=sQuery(id+"F0.wireOp",EDGE,"E24.filletArc");Q0=makeQuery(id+"F2.boolean.opBoolean","SPLIT",FACE,{"disambiguationData":[TD([makeQuery(id+"F1.opExtrude","SWEPT_FACE",FACE,{"disambiguationData":[OSD([subQ6])]})])],"derivedFrom":makeQuery(id+"F1.opExtrude","CAP_FACE",FACE,{"disambiguationData":[OSD([subQ6,subQ8,subQ9,subQ7,subQ4,subQ3,subQ2,subQ1,subQ0,subQ5,subQ10,subQ11])],"isStart":true})});}
            var sketch = newSketch(context, id + "F16", { "sketchPlane" : qUnion([Q0])});
            skLineSegment(sketch, "E79", {"start": v(0, 74.25) * mm, "end": v(0, 104.25) * mm});
            skCircle(sketch, "E80", {"center": v(0, 104.25) * mm, "radius": 6.3 * mm});
            skLineSegment(sketch, "E81", {"start": v(-53.36, 74.25) * mm, "end": v(-53.36, 79.3) * mm});
            skLineSegment(sketch, "E82", {"start": v(-53.36, 74.25) * mm, "end": v(-53.36, 92.25) * mm});
            skLineSegment(sketch, "E83", {"start": v(-34.77, 74.25) * mm, "end": v(-16.77, 92.25) * mm});
            skLineSegment(sketch, "E84", {"start": v(35.66, 74.25) * mm, "end": v(17.66, 92.25) * mm});
            skArc(sketch, "E85", {"start": v(17.66, 92.25) * mm, "mid": v(0.45, 118.21) * mm, "end": v(-16.77, 92.25) * mm});
            skPoint(sketch, "E86.startSnap0", {"position": v(-74.25, 0) * mm});
            skPoint(sketch, "E86.endSnap0", {"position": v(60, 0) * mm});
            skLineSegment(sketch, "E87.MirrorCS", {"start": v(0, -74.25) * mm, "end": v(0, -104.25) * mm});
            skLineSegment(sketch, "E88.MirrorCS", {"start": v(-34.77, -74.25) * mm, "end": v(-16.77, -92.25) * mm});
            skCircle(sketch, "E89.MirrorC", {"center": v(0, -104.25) * mm, "radius": 6.3 * mm});
            skArc(sketch, "E90.MirrorCS", {"start": v(17.66, -92.25) * mm, "mid": v(0.45, -118.21) * mm, "end": v(-16.77, -92.25) * mm});
            skLineSegment(sketch, "E91.MirrorCS", {"start": v(35.66, -74.25) * mm, "end": v(17.66, -92.25) * mm});
            skSolve(sketch);
        }
        {
            var Q0;
            Q0=makeQuery(id+"F16.imprint","IMPRINT",FACE,{"disambiguationData":[TD([[makeQuery(id+"F16.imprint","IMPRINT",EDGE,{"derivedFrom":sQuery(id+"F16.wireOp",EDGE,"E80")}),-1.0]])]});
            var Q1;
            Q1=makeQuery(id+"F16.imprint","IMPRINT",FACE,{"disambiguationData":[TD([[makeQuery(id+"F16.imprint","IMPRINT",EDGE,{"derivedFrom":makeQuery(id+"F1.opExtrude","CAP_EDGE",EDGE,{"disambiguationData":[OSD([sQuery(id+"F0.wireOp",EDGE,"E1.left")])],"isStart":true})}),-1.0]])]});
            var Q2;
            {var subQ3=sQuery(id+"F16.wireOp",EDGE,"E88.MirrorCS");Q2=makeQuery(id+"F16.imprint","IMPRINT",FACE,{"disambiguationData":[TD([[makeQuery(id+"F16.imprint","IMPRINT",EDGE,{"derivedFrom":subQ3}),1.0]])]});}
            extrude(context, id + "F17", {"entities" : qUnion([Q0, Q1, Q2]), "depth" : 10 * mm});
        }
    });
